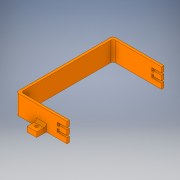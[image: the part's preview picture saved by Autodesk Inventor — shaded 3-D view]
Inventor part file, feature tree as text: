
AUTODESK INVENTOR PART (.ipt)
format: ipt  version: 2019 (Build 230136000, 136)  size: 204,288 bytes
history: native  units: in
note: dims shown in document units (in); Inventor stores cm internally (conversion verified against a paired STEP export)
features: sketch x4, extrude x3, fillet x2, hole x1, plane x1, mirror x1, projected_geometry x1
ambient origin geometry x8: Origin, YZ Plane, XZ Plane, XY Plane, X Axis, Y Axis, Z Axis, Center Point
bodies: Solid1 (feature_tree)
feature tree (13):
  extrude  "Extrusion1"  Depth=0.125in
  extrude  "Extrusion3"  Depth=4.75in
  extrude  "Extrusion4"  Depth=1.0in TaperAngle=0.0deg
  hole  "Hole1"  [1 undecoded]
  plane  "Work Plane1"
  mirror  "Mirror1"
  fillet  "Fillet1"  Radius=0.25in
  fillet  "Fillet2"  Radius=0.1in
  sketch  "Sketch1"  dims[d0=0.125in d1=0.125in]
  sketch  "Sketch2"  dims[d2=0.125in d3=4.75in]
  sketch  "Sketch3"  dims[d4=2.5in d5=1.0in d6=0.0in]
  sketch  "Sketch4"  dims[d9=0.1in d10=0.1in d11=0.25in d12=0.1in d13=0.075in d14=0.45in d15=1.0in d16=0.275in d17=0.1in d18=0.1in d19=0.5in d20=0.5in d21=1.0in d22=0.0in d26=0.5in d27=0.5in d28=2.625in d29=1.0625in d30=0.0in d31=0.25in d32=0.0in d33=0.15in d34=0.28in d35=0.375in d36=0.25in d37=0.5635in d38=0.28in d39=0.8108in d40=0.125in d41=0.125in]
  projected_geometry  "Projected Loop1"
note: 1 required parameter value undecoded (feature->parameter linkage not recoverable at this tier; creation-order binding heuristic only, values carry confidence <= 0.55)
